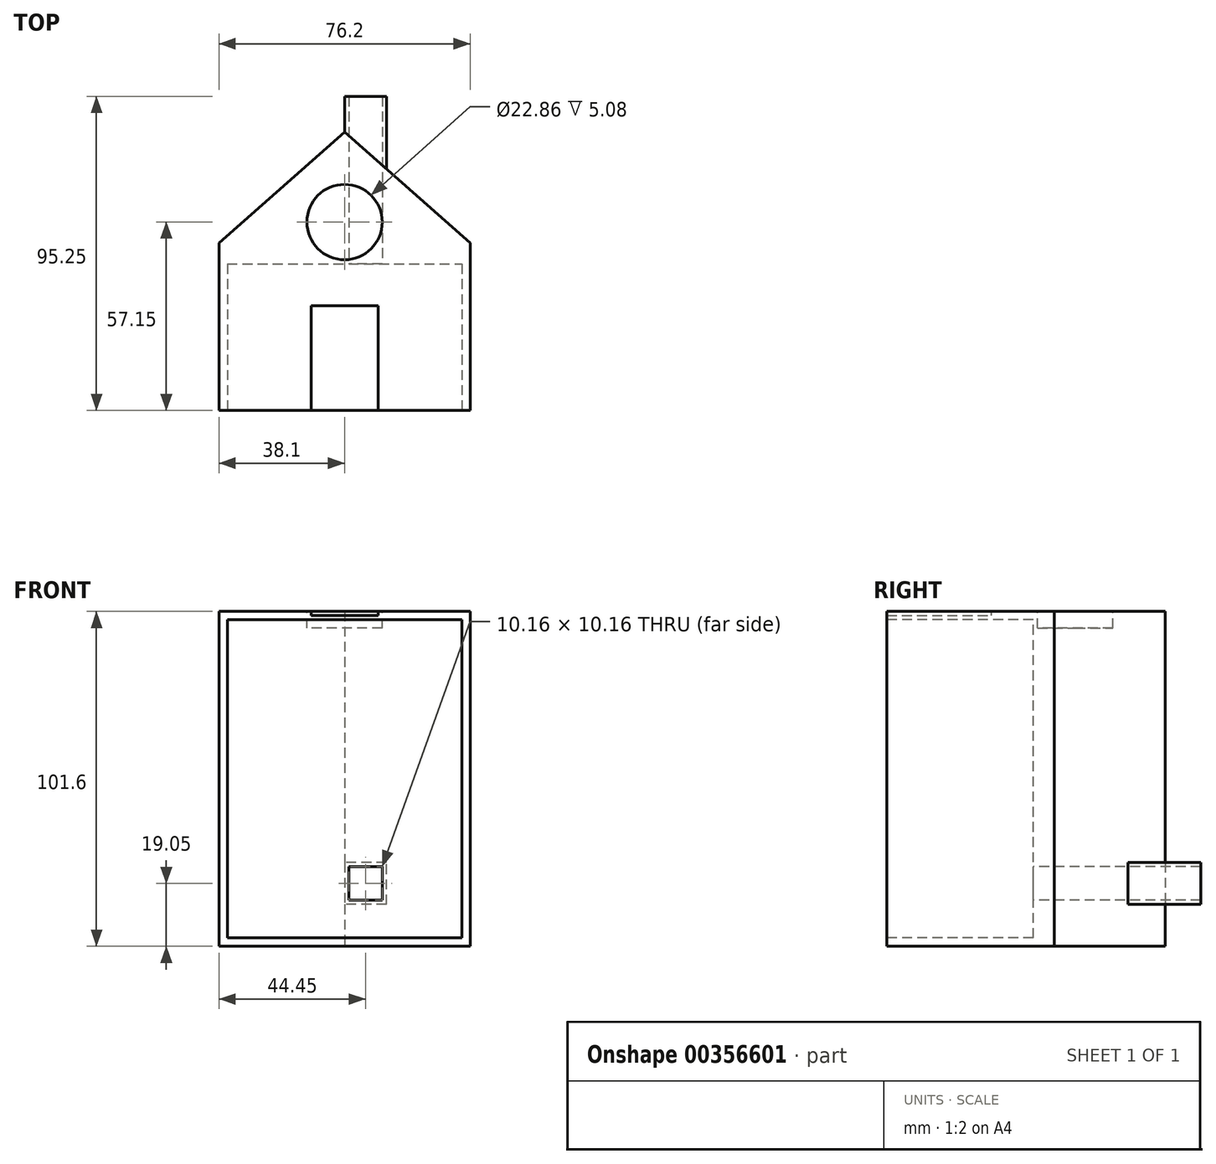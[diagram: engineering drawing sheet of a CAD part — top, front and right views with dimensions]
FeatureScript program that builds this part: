
annotation { "Feature Type Name" : "Feature", "Feature Type Description" : "" }
export const myFeature = defineFeature(function(context is Context, id is Id, definition is map)
    precondition{}
    {
        {
            var Q0;
            Q0=qCreatedBy(makeId("Top.planeOp"),FACE);
            var sketch = newSketch(context, id + "F0", { "sketchPlane" : qUnion([Q0])});
            skLineSegment(sketch, "E0.bottom", {"start": v(0, 0) * mm, "end": v(76.2, 0) * mm});
            skLineSegment(sketch, "E0.top", {"start": v(0, 50.8) * mm, "end": v(76.2, 50.8) * mm});
            skLineSegment(sketch, "E0.left", {"start": v(0, 0) * mm, "end": v(0, 50.8) * mm});
            skLineSegment(sketch, "E0.right", {"start": v(76.2, 0) * mm, "end": v(76.2, 50.8) * mm});
            skLineSegment(sketch, "E1", {"start": v(0, 50.8) * mm, "end": v(38.1, 84.4) * mm});
            skLineSegment(sketch, "E2", {"start": v(38.1, 84.4) * mm, "end": v(76.2, 50.8) * mm});
            skLineSegment(sketch, "E3.bottom", {"start": v(-101.6, 0) * mm, "end": v(-177.8, 0) * mm});
            skLineSegment(sketch, "E3.top", {"start": v(-101.6, 50.8) * mm, "end": v(-177.8, 50.8) * mm});
            skLineSegment(sketch, "E3.left", {"start": v(-101.6, 0) * mm, "end": v(-101.6, 50.8) * mm});
            skLineSegment(sketch, "E3.right", {"start": v(-177.8, 0) * mm, "end": v(-177.8, 50.8) * mm});
            skLineSegment(sketch, "E4.bottom", {"start": v(152.4, 0) * mm, "end": v(158.75, 0) * mm});
            skLineSegment(sketch, "E4.top", {"start": v(152.4, 50.8) * mm, "end": v(158.75, 50.8) * mm});
            skLineSegment(sketch, "E4.left", {"start": v(152.4, 0) * mm, "end": v(152.4, 50.8) * mm});
            skLineSegment(sketch, "E4.right", {"start": v(158.75, 0) * mm, "end": v(158.75, 50.8) * mm});
            skSolve(sketch);
        }
        {
            var Q0;
            Q0=makeQuery(id+"F0.imprint","IMPRINT",FACE,{"disambiguationData":[TD([[makeQuery(id+"F0.imprint","IMPRINT",EDGE,{"derivedFrom":sQuery(id+"F0.wireOp",EDGE,"E0.top")}),1.0]])]});
            var Q1;
            Q1=makeQuery(id+"F0.imprint","IMPRINT",FACE,{"disambiguationData":[TD([[makeQuery(id+"F0.imprint","IMPRINT",EDGE,{"derivedFrom":sQuery(id+"F0.wireOp",EDGE,"E0.bottom")}),1.0]])]});
            extrude(context, id + "F1", {"entities" : qUnion([Q0, Q1]), "depth" : 101.6 * mm});
        }
        {
            var Q0;
            Q0=makeQuery(id+"F1.opExtrude","CAP_FACE",FACE,{"disambiguationData":[OSD([sQuery(id+"F0.wireOp",EDGE,"E0.bottom"),sQuery(id+"F0.wireOp",EDGE,"E0.left"),sQuery(id+"F0.wireOp",EDGE,"E0.right"),sQuery(id+"F0.wireOp",EDGE,"E1"),sQuery(id+"F0.wireOp",EDGE,"E2")])],"isStart":false});
            var sketch = newSketch(context, id + "F2", { "sketchPlane" : qUnion([Q0])});
            skLineSegment(sketch, "E5.bottom", {"start": v(48.26, 0) * mm, "end": v(27.94, 0) * mm});
            skLineSegment(sketch, "E5.top", {"start": v(48.26, 31.75) * mm, "end": v(27.94, 31.75) * mm});
            skLineSegment(sketch, "E5.left", {"start": v(48.26, 0) * mm, "end": v(48.26, 31.75) * mm});
            skLineSegment(sketch, "E5.right", {"start": v(27.94, 0) * mm, "end": v(27.94, 31.75) * mm});
            skCircle(sketch, "E6", {"center": v(38.1, 57.15) * mm, "radius": 11.43 * mm});
            skSolve(sketch);
        }
        {
            var Q0;
            Q0=makeQuery(id+"F1.opExtrude","SWEPT_FACE",FACE,{"disambiguationData":[OSD([sQuery(id+"F0.wireOp",EDGE,"E0.bottom")])]});
            var sketch = newSketch(context, id + "F3", { "sketchPlane" : qUnion([Q0])});
            skLineSegment(sketch, "E7.bottom", {"start": v(2.54, 2.54) * mm, "end": v(73.66, 2.54) * mm});
            skLineSegment(sketch, "E7.top", {"start": v(2.54, 99.06) * mm, "end": v(73.66, 99.06) * mm});
            skLineSegment(sketch, "E7.left", {"start": v(2.54, 2.54) * mm, "end": v(2.54, 99.06) * mm});
            skLineSegment(sketch, "E7.right", {"start": v(73.66, 2.54) * mm, "end": v(73.66, 99.06) * mm});
            skSolve(sketch);
        }
        {
            var Q0;
            Q0=qSketchRegion(id+"F3",true);
            extrude(context, id + "F4", {"entities" : qUnion([Q0]), "operationType" : NewBodyOperationType.REMOVE, "oppositeDirection" : true, "depth" : 44.45 * mm});
        }
        {
            var Q0;
            Q0=makeQuery(id+"F2.imprint","IMPRINT",FACE,{"disambiguationData":[TD([[makeQuery(id+"F2.imprint","IMPRINT",EDGE,{"derivedFrom":sQuery(id+"F2.wireOp",EDGE,"E6")}),1.0]])]});
            extrude(context, id + "F5", {"entities" : qUnion([Q0]), "operationType" : NewBodyOperationType.REMOVE, "oppositeDirection" : true, "depth" : 5.08 * mm});
        }
        {
            var Q0;
            Q0=qSketchRegion(id+"F2",true);
            extrude(context, id + "F6", {"entities" : qUnion([Q0]), "operationType" : NewBodyOperationType.REMOVE, "oppositeDirection" : true, "depth" : 1.27 * mm});
        }
        {
            var Q0;
            Q0=makeQuery(id+"F4.boolean.opBoolean","COPY",FACE,{"derivedFrom":makeQuery(id+"F4.opExtrude","CAP_FACE",FACE,{"disambiguationData":[OSD([sQuery(id+"F3.wireOp",EDGE,"E7.bottom"),sQuery(id+"F3.wireOp",EDGE,"E7.top"),sQuery(id+"F3.wireOp",EDGE,"E7.left"),sQuery(id+"F3.wireOp",EDGE,"E7.right")])],"isStart":false})});
            var sketch = newSketch(context, id + "F7", { "sketchPlane" : qUnion([Q0])});
            skLineSegment(sketch, "E8.bottom", {"start": v(38.1, 25.4) * mm, "end": v(50.8, 25.4) * mm});
            skLineSegment(sketch, "E8.top", {"start": v(38.1, 12.7) * mm, "end": v(50.8, 12.7) * mm});
            skLineSegment(sketch, "E8.left", {"start": v(38.1, 25.4) * mm, "end": v(38.1, 12.7) * mm});
            skLineSegment(sketch, "E8.right", {"start": v(50.8, 25.4) * mm, "end": v(50.8, 12.7) * mm});
            skLineSegment(sketch, "E9.bottom", {"start": v(49.53, 13.97) * mm, "end": v(39.37, 13.97) * mm});
            skLineSegment(sketch, "E9.top", {"start": v(49.53, 24.13) * mm, "end": v(39.37, 24.13) * mm});
            skLineSegment(sketch, "E9.left", {"start": v(49.53, 13.97) * mm, "end": v(49.53, 24.13) * mm});
            skLineSegment(sketch, "E9.right", {"start": v(39.37, 13.97) * mm, "end": v(39.37, 24.13) * mm});
            skSolve(sketch);
        }
        {
            var Q0;
            Q0=qSketchRegion(id+"F7",true);
            extrude(context, id + "F8", {"entities" : qUnion([Q0]), "operationType" : NewBodyOperationType.ADD, "oppositeDirection" : true, "depth" : 50.8 * mm});
        }
        {
            var Q0;
            Q0=makeQuery(id+"F7.imprint","IMPRINT",FACE,{"disambiguationData":[TD([[makeQuery(id+"F7.imprint","IMPRINT",EDGE,{"derivedFrom":sQuery(id+"F7.wireOp",EDGE,"E9.bottom")}),-1.0]])]});
            extrude(context, id + "F9", {"entities" : qUnion([Q0]), "operationType" : NewBodyOperationType.REMOVE, "endBound" : BoundingType.THROUGH_ALL, "oppositeDirection" : true, "depth" : 25.4 * mm});
        }
    });
